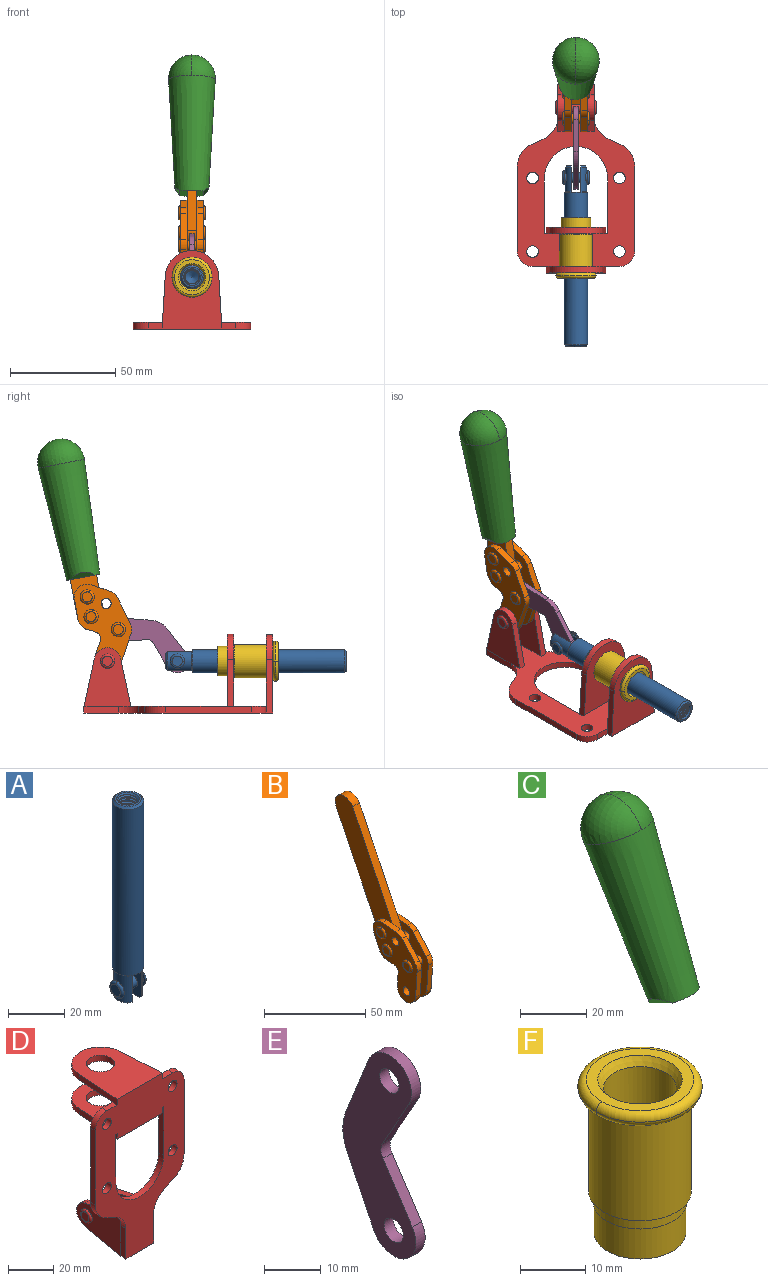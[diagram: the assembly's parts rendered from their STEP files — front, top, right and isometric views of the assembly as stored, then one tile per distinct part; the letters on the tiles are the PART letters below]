
ASSEMBLY  parts=6 mates=6
PART A: 48 faces, bbox 12.6x11.1x86.1 mm
  f0: torus R=2.41mm, axis (-1,0,0), area 15mm2, adj f30,f32,f34
  f1: torus R=2.41mm, axis (-1,0,0), area 15mm2, adj f29,f31,f33
  f2: cylinder r=5.54mm len=72.39mm, axis (0,0,1), area 2518.5mm2, adj f3,f4,f42,f43
  f3: cone r=5.54mm half-angle=45deg, axis (0,0,1), area 7.6mm2, adj f2,f5,f41
  f4: cone r=5.54mm half-angle=45deg, axis (0,0,-1), area 34.9mm2, adj f2,f39
  f5: cylinder r=5.08mm len=11.48mm, axis (0,0,1), area 108.3mm2, adj f3,f7,f8,f41
  f6: cylinder r=2.41mm len=4.83mm, axis (-1,0,0), area 71.2mm2, adj f40,f41
  f7: cylinder r=2.41mm len=4.83mm, axis (-1,0,0), area 7.6mm2, adj f5,f34
  f8: cone r=5.08mm half-angle=45deg, axis (0,0,1), area 10.6mm2, adj f5,f37,f41
  f9: cone r=3.98mm half-angle=45deg, axis (0,0,1), area 17.6mm2, adj f27,f39,f45,f46,f47
  f10: cylinder r=2.41mm len=4.83mm, axis (-1,0,0), area 7.6mm2, adj f33,f38
  f11: cylinder r=3.2mm len=6.4mm, axis (0,0,1), area 78.4mm2, adj f12,f28,f44,f45,f47
  f12: cylinder r=3.2mm len=6.4mm, axis (0,0,1), area 10.5mm2, adj f11,f13,f45,f47
  f13: cylinder r=3.2mm len=6.4mm, axis (0,0,1), area 10.5mm2, adj f12,f14,f45,f47
  f14: cylinder r=3.2mm len=6.4mm, axis (0,0,1), area 10.5mm2, adj f13,f15,f45,f47
  f15: cylinder r=3.2mm len=6.4mm, axis (0,0,1), area 10.5mm2, adj f14,f16,f45,f47
  f16: cylinder r=3.2mm len=6.4mm, axis (0,0,1), area 10.5mm2, adj f15,f17,f45,f47
  f17: cylinder r=3.2mm len=6.4mm, axis (0,0,1), area 10.5mm2, adj f16,f18,f45,f47
  f18: cylinder r=3.2mm len=6.4mm, axis (0,0,1), area 10.5mm2, adj f17,f19,f45,f47
  f19: cylinder r=3.2mm len=6.4mm, axis (0,0,1), area 10.5mm2, adj f18,f20,f45,f47
  f20: cylinder r=3.2mm len=6.4mm, axis (0,0,1), area 10.5mm2, adj f19,f21,f45,f47
  f21: cylinder r=3.2mm len=6.4mm, axis (0,0,1), area 10.5mm2, adj f20,f22,f45,f47
  f22: cylinder r=3.2mm len=6.4mm, axis (0,0,1), area 10.5mm2, adj f21,f23,f45,f47
  f23: cylinder r=3.2mm len=6.4mm, axis (0,0,1), area 10.5mm2, adj f22,f24,f45,f47
  f24: cylinder r=3.2mm len=6.4mm, axis (0,0,1), area 10.5mm2, adj f23,f25,f45,f47
  f25: cylinder r=3.2mm len=6.4mm, axis (0,0,1), area 10.5mm2, adj f24,f26,f45,f47
  f26: cylinder r=3.2mm len=6.4mm, axis (0,0,1), area 10.5mm2, adj f25,f27,f45,f47
  f27: cylinder r=3.2mm len=6.4mm, axis (0,0,1), area 7.4mm2, adj f9,f26,f45,f47
  f28: cone r=3.2mm half-angle=60deg, axis (0,0,1), area 37.2mm2, adj f11
  f29: plane 4.83x4.83mm, normal (-1,0,0), area 18.3mm2, adj f1,f31
  f30: plane 4.83x4.83mm, normal (1,0,0), area 18.3mm2, adj f0,f32
  f31: torus R=2.41mm, axis (-1,0,0), area 15mm2, adj f1,f29,f33
  f32: torus R=2.41mm, axis (-1,0,0), area 15mm2, adj f0,f30,f34
  f33: plane 6.83x6.83mm, normal (1,0,0), area 18.3mm2, adj f1,f10,f31
  f34: plane 6.83x6.83mm, normal (-1,0,0), area 18.3mm2, adj f0,f7,f32
  f35: cone r=5.08mm half-angle=45deg, axis (0,0,1), area 10.6mm2, adj f36,f38,f40
  f36: plane 7.25x1.97mm, normal (0,0,-1), area 10mm2, adj f35,f40
  f37: plane 7.25x1.97mm, normal (0,0,-1), area 10mm2, adj f8,f41
  f38: cylinder r=5.08mm len=11.48mm, axis (0,0,1), area 108.3mm2, adj f10,f35,f40,f42
  f39: plane 9.55x9.55mm, normal (0,0,1), area 22mm2, adj f4,f9
  f40: plane 12.76x10.09mm, normal (1,0,0), area 95.7mm2, adj f6,f35,f36,f38,f42,f43
  f41: plane 12.76x10.09mm, normal (-1,0,0), area 95.7mm2, adj f3,f5,f6,f8,f37,f43
  f42: cone r=5.54mm half-angle=45deg, axis (0,0,1), area 7.6mm2, adj f2,f38,f40
  f43: plane 11.07x4.7mm, normal (0,0,-1), area 50.4mm2, adj f2,f40,f41
  f44: plane 0.89x0.62mm, normal (-1,0,0), area 0.3mm2, adj f11,f45,f46,f47
  f45: bspline ~24.8x7.63mm, area 266.6mm2, adj f9,f11,f12,f13,f14,f15,f16,f17
  f46: bspline ~24.87x7.63mm, area 73.6mm2, adj f9,f44,f45,f47
  f47: bspline ~24.98x7.63mm, area 272.5mm2, adj f9,f11,f12,f13,f14,f15,f16,f17
PART B: 59 faces, bbox 12.9x60.2x99.6 mm
  f0: torus R=2.39mm, axis (-1,0,0), area 14.9mm2, adj f20,f43,f51
  f1: torus R=2.39mm, axis (-1,0,0), area 14.9mm2, adj f19,f42,f51
  f2: torus R=2.39mm, axis (-1,0,0), area 14.9mm2, adj f18,f35,f51
  f3: torus R=2.39mm, axis (-1,0,0), area 14.9mm2, adj f14,f17,f23
  f4: torus R=2.39mm, axis (-1,0,0), area 14.9mm2, adj f13,f16,f23
  f5: torus R=2.39mm, axis (-1,0,0), area 14.9mm2, adj f12,f15,f23
  f6: cylinder r=2.39mm len=4.78mm, axis (1,0,0), area 46.5mm2, adj f48,f50,f51
  f7: cylinder r=2.39mm len=4.78mm, axis (1,0,0), area 46.5mm2, adj f50,f51
  f8: cylinder r=6.35mm len=12.68mm, axis (1,0,0), area 61.8mm2, adj f38,f39,f50,f51
  f9: cylinder r=2.39mm len=4.78mm, axis (-1,0,0), area 70.5mm2, adj f46,f50
  f10: cylinder r=2.39mm len=4.78mm, axis (-1,0,0), area 46.5mm2, adj f23,f45,f46
  f11: cylinder r=2.39mm len=4.78mm, axis (-1,0,0), area 46.5mm2, adj f23,f46
  f12: plane 4.78x4.78mm, normal (1,0,0), area 17.9mm2, adj f5,f15
  f13: plane 4.78x4.78mm, normal (1,0,0), area 17.9mm2, adj f4,f16
  f14: plane 4.78x4.78mm, normal (1,0,0), area 17.9mm2, adj f3,f17
  f15: torus R=2.39mm, axis (-1,0,0), area 14.9mm2, adj f5,f12,f23
  f16: torus R=2.39mm, axis (-1,0,0), area 14.9mm2, adj f4,f13,f23
  f17: torus R=2.39mm, axis (-1,0,0), area 14.9mm2, adj f3,f14,f23
  f18: plane 4.78x4.78mm, normal (-1,0,0), area 17.9mm2, adj f2,f35
  f19: plane 4.78x4.78mm, normal (-1,0,0), area 17.9mm2, adj f1,f42
  f20: plane 4.78x4.78mm, normal (-1,0,0), area 17.9mm2, adj f0,f43
  f21: plane 2.26x0.2mm, normal (1,0,0), area 0.2mm2, adj f31,f44
  f22: plane 2.26x0.2mm, normal (-1,0,0), area 0.2mm2, adj f41,f44
  f23: plane 39.37x30.77mm, normal (1,0,0), area 565.5mm2, adj f3,f4,f5,f10,f11,f15,f16,f17
  f24: cylinder r=6.1mm len=4.15mm, axis (-1,0,0), area 14.7mm2, adj f23,f25,f32,f46
  f25: plane 10.25x9.01mm, normal (0,-0.75,0.66), area 42.3mm2, adj f23,f24,f26,f46
  f26: cylinder r=6.35mm len=4.64mm, axis (-1,0,0), area 15.6mm2, adj f23,f25,f27,f46
  f27: plane 15.84x3.1mm, normal (0,-1,-0.07), area 49.2mm2, adj f23,f26,f28,f46
  f28: cylinder r=6.35mm len=12.68mm, axis (-1,0,0), area 61.8mm2, adj f23,f27,f29,f46
  f29: plane 8.11x3.1mm, normal (0,1,0.07), area 25.2mm2, adj f23,f28,f30,f46
  f30: cylinder r=3.05mm len=3.25mm, axis (-1,0,0), area 14.8mm2, adj f23,f29,f31,f46
  f31: plane 5.99x3.1mm, normal (0,0.07,-1), area 18.6mm2, adj f21,f23,f30,f44,f46
  f32: plane 9.5x3.1mm, normal (0,-0.07,1), area 29.5mm2, adj f23,f24,f33,f46,f47
  f33: cylinder r=6.1mm len=8.63mm, axis (-1,0,0), area 39.1mm2, adj f23,f32,f34,f47
  f34: plane 8.65x3.96mm, normal (0,0.91,-0.42), area 29.5mm2, adj f23,f33,f44,f47
  f35: torus R=2.39mm, axis (-1,0,0), area 14.9mm2, adj f2,f18,f51
  f36: plane 10.25x9.01mm, normal (0,-0.75,0.66), area 42.3mm2, adj f37,f49,f50,f51
  f37: cylinder r=6.35mm len=4.64mm, axis (1,0,0), area 15.6mm2, adj f36,f38,f50,f51
  f38: plane 15.84x3.1mm, normal (0,-1,-0.07), area 49.2mm2, adj f8,f37,f50,f51
  f39: plane 8.11x3.1mm, normal (0,1,0.07), area 25.2mm2, adj f8,f40,f50,f51
  f40: cylinder r=3.05mm len=3.25mm, axis (1,0,0), area 14.8mm2, adj f39,f41,f50,f51
  f41: plane 5.99x3.1mm, normal (0,0.07,-1), area 18.6mm2, adj f22,f40,f44,f50,f51
  f42: torus R=2.39mm, axis (-1,0,0), area 14.9mm2, adj f1,f19,f51
  f43: torus R=2.39mm, axis (-1,0,0), area 14.9mm2, adj f0,f20,f51
  f44: cylinder r=6.35mm len=12.12mm, axis (-1,0,0), area 128.9mm2, adj f21,f22,f23,f31,f34,f41,f46,f47
  f45: plane 2.65x1.35mm, normal (1,0,0), area 1mm2, adj f10,f55
  f46: plane 39.08x20.42mm, normal (-1,0,0), area 412.5mm2, adj f9,f10,f11,f24,f25,f26,f27,f28
  f47: plane 77.62x39.82mm, normal (1,0,0), area 850mm2, adj f32,f33,f34,f44,f53,f54,f55
  f48: plane 2.65x1.35mm, normal (-1,0,0), area 1mm2, adj f6,f55
  f49: cylinder r=6.1mm len=4.15mm, axis (1,0,0), area 14.7mm2, adj f36,f50,f51,f56
  f50: plane 39.08x20.42mm, normal (1,0,0), area 412.5mm2, adj f6,f7,f8,f9,f36,f37,f38,f39
  f51: plane 39.37x30.77mm, normal (-1,0,0), area 565.5mm2, adj f0,f1,f2,f6,f7,f8,f35,f36
  f52: plane 8.65x3.96mm, normal (0,0.91,-0.42), area 29.5mm2, adj f44,f51,f57,f58
  f53: plane 68.49x33.4mm, normal (0,0.9,-0.44), area 358.1mm2, adj f44,f47,f54,f58
  f54: cylinder r=6.35mm len=12.06mm, axis (1,0,0), area 93.7mm2, adj f47,f53,f55,f58
  f55: plane 68.49x33.4mm, normal (0,-0.9,0.44), area 358.1mm2, adj f44,f45,f46,f47,f48,f50,f54,f58
  f56: plane 9.5x3.1mm, normal (0,-0.07,1), area 29.5mm2, adj f49,f50,f51,f57,f58
  f57: cylinder r=6.1mm len=8.63mm, axis (1,0,0), area 39.1mm2, adj f51,f52,f56,f58
  f58: plane 77.62x39.82mm, normal (-1,0,0), area 850mm2, adj f44,f52,f53,f54,f55,f56,f57
PART C: 11 faces, bbox 22.3x42.6x64.5 mm
  f0: sphere r=11.13mm, area 411.4mm2, adj f1,f8
  f1: cone r=11.11mm half-angle=3.3deg, axis (0,0.44,0.9), area 3251.8mm2, adj f0,f7,f8,f9,f10
  f2: cylinder r=6.16mm len=11.7mm, axis (1,0,0), area 89.5mm2, adj f3,f4,f5,f6
  f3: plane 60.23x36.75mm, normal (-1,0,0), area 763.6mm2, adj f2,f4,f6,f10
  f4: plane 51.37x25.05mm, normal (0,0.9,-0.44), area 264.2mm2, adj f2,f3,f5,f10
  f5: plane 60.23x36.75mm, normal (1,0,0), area 763.6mm2, adj f2,f4,f6,f10
  f6: plane 51.37x25.05mm, normal (0,-0.9,0.44), area 264.2mm2, adj f2,f3,f5,f10
  f7: plane 9.95x5.95mm, normal (0.71,-0.31,-0.64), area 25.8mm2, adj f1,f10
  f8: sphere r=11.13mm, area 411.4mm2, adj f0,f1
  f9: plane 9.95x5.95mm, normal (-0.71,-0.31,-0.64), area 25.8mm2, adj f1,f10
  f10: plane 14.27x11.38mm, normal (0,-0.44,-0.9), area 106.7mm2, adj f1,f3,f4,f5,f6,f7,f9
PART D: 55 faces, bbox 55.7x37.4x89.8 mm
  f0: torus R=2.41mm, axis (-1,0,0), area 15mm2, adj f11,f15,f25
  f1: torus R=2.41mm, axis (-1,0,0), area 15mm2, adj f10,f12,f22
  f2: cylinder r=2.78mm len=5.56mm, axis (0,-1,0), area 54.2mm2, adj f30,f54
  f3: cylinder r=14.99mm len=29.97mm, axis (0,-1,0), area 145.9mm2, adj f30,f49,f53,f54
  f4: cylinder r=2.78mm len=5.56mm, axis (0,-1,0), area 54.2mm2, adj f30,f54
  f5: cylinder r=2.78mm len=5.56mm, axis (0,-1,0), area 54.2mm2, adj f30,f54
  f6: cylinder r=2.78mm len=5.56mm, axis (0,-1,0), area 54.2mm2, adj f30,f54
  f7: cylinder r=6.35mm len=12.7mm, axis (0,0,1), area 123.6mm2, adj f27,f51
  f8: cylinder r=6.35mm len=12.7mm, axis (0,0,-1), area 124.7mm2, adj f21,f35
  f9: cylinder r=2.41mm len=11.18mm, axis (-1,0,0), area 169.4mm2, adj f16,f19
  f10: plane 4.83x4.83mm, normal (1,0,0), area 18.3mm2, adj f1,f12
  f11: plane 4.83x4.83mm, normal (-1,0,0), area 18.3mm2, adj f0,f15
  f12: torus R=2.41mm, axis (-1,0,0), area 15mm2, adj f1,f10,f22
  f13: cylinder r=6.35mm len=12.41mm, axis (1,0,0), area 53.4mm2, adj f18,f19,f22,f23
  f14: cylinder r=6.35mm len=12.41mm, axis (-1,0,0), area 53.4mm2, adj f16,f17,f24,f25
  f15: torus R=2.41mm, axis (-1,0,0), area 15mm2, adj f0,f11,f25
  f16: plane 27.86x22.35mm, normal (1,0,0), area 425.4mm2, adj f9,f14,f17,f24,f30
  f17: plane 22.86x4.97mm, normal (0,0.21,0.98), area 72.5mm2, adj f14,f16,f25,f30
  f18: plane 22.86x4.97mm, normal (0,0.21,0.98), area 72.5mm2, adj f13,f19,f22,f30
  f19: plane 27.86x22.35mm, normal (-1,0,0), area 425.4mm2, adj f9,f13,f18,f23,f30
  f20: cylinder r=12.7mm len=25.35mm, axis (0,0,-1), area 119.8mm2, adj f21,f34,f35,f36
  f21: plane 34.21x28.07mm, normal (0,0,-1), area 702.4mm2, adj f8,f20,f30,f34,f36
  f22: plane 27.96x22.45mm, normal (1,0,0), area 407.2mm2, adj f1,f12,f13,f18,f23,f30,f42,f43
  f23: plane 22.86x4.97mm, normal (0,0.21,-0.98), area 72.5mm2, adj f13,f19,f22,f44
  f24: plane 22.86x4.97mm, normal (0,0.21,-0.98), area 72.5mm2, adj f14,f16,f25,f44
  f25: plane 27.86x22.35mm, normal (-1,0,0), area 407.1mm2, adj f0,f14,f15,f17,f24,f30,f45,f46
  f26: plane 3.1x0.95mm, normal (0,0,-1), area 2.7mm2, adj f30,f49,f50,f54
  f27: plane 34.21x28.07mm, normal (0,0,1), area 702.4mm2, adj f7,f28,f30,f50,f52
  f28: cylinder r=12.7mm len=25.35mm, axis (0,0,1), area 118.8mm2, adj f27,f50,f51,f52
  f29: plane 3.1x0.95mm, normal (0,0,-1), area 2.7mm2, adj f30,f52,f53,f54
  f30: plane 86.54x55.63mm, normal (0,1,0), area 2362.9mm2, adj f2,f3,f4,f5,f6,f16,f17,f18
  f31: plane 40.56x3.1mm, normal (-1,0,0), area 125.7mm2, adj f30,f32,f48,f54
  f32: cylinder r=7.11mm len=7.11mm, axis (0,-1,0), area 34.6mm2, adj f30,f31,f33,f54
  f33: plane 6.67x3.1mm, normal (0,0,1), area 20.4mm2, adj f30,f32,f34,f54
  f34: plane 25.39x3.13mm, normal (-1,0.06,0), area 79.5mm2, adj f20,f21,f33,f35,f54
  f35: plane 37.31x28.45mm, normal (0,0,1), area 789.9mm2, adj f8,f20,f34,f36,f54
  f36: plane 25.39x3.13mm, normal (1,0.06,0), area 79.5mm2, adj f20,f21,f35,f37,f54
  f37: plane 6.67x3.1mm, normal (0,0,1), area 20.4mm2, adj f30,f36,f38,f54
  f38: cylinder r=7.11mm len=7.11mm, axis (0,-1,0), area 34.6mm2, adj f30,f37,f39,f54
  f39: plane 40.56x3.1mm, normal (1,0,0), area 125.7mm2, adj f30,f38,f40,f54
  f40: cylinder r=11.18mm len=10.16mm, axis (0,-1,0), area 39.5mm2, adj f30,f39,f41,f54
  f41: plane 6.09x3.1mm, normal (0.42,0,-0.91), area 20.8mm2, adj f30,f40,f42,f54
  f42: cylinder r=11.18mm len=9.41mm, axis (0,-1,0), area 37.2mm2, adj f22,f30,f41,f43,f54
  f43: plane 16.5x3.1mm, normal (1,0,0), area 51.1mm2, adj f22,f42,f44,f54
  f44: plane 17.37x3.1mm, normal (0,0,-1), area 53.8mm2, adj f23,f24,f30,f43,f45,f54
  f45: plane 16.5x3.1mm, normal (-1,0,0), area 51.1mm2, adj f25,f44,f46,f54
  f46: cylinder r=11.18mm len=9.41mm, axis (0,-1,0), area 37.2mm2, adj f25,f30,f45,f47,f54
  f47: plane 6.09x3.1mm, normal (-0.42,0,-0.91), area 20.8mm2, adj f30,f46,f48,f54
  f48: cylinder r=11.18mm len=10.16mm, axis (0,-1,0), area 39.5mm2, adj f30,f31,f47,f54
  f49: plane 26.54x3.1mm, normal (-1,0,0), area 82.3mm2, adj f3,f26,f30,f54
  f50: plane 25.39x3.1mm, normal (1,0.06,0), area 78.8mm2, adj f26,f27,f28,f51,f54
  f51: plane 37.31x28.45mm, normal (0,0,-1), area 789.9mm2, adj f7,f28,f50,f52,f54
  f52: plane 25.39x3.1mm, normal (-1,0.06,0), area 78.8mm2, adj f27,f28,f29,f51,f54
  f53: plane 26.54x3.1mm, normal (1,0,0), area 82.3mm2, adj f3,f29,f30,f54
  f54: plane 89.66x55.63mm, normal (0,-1,0), area 2678.5mm2, adj f2,f3,f4,f5,f6,f26,f29,f31
PART E: 12 faces, bbox 2.3x18.2x42.8 mm
  f0: cylinder r=2.4mm len=4.8mm, axis (1,0,0), area 34.9mm2, adj f4,f11
  f1: cylinder r=10.41mm len=8.47mm, axis (1,0,0), area 20.2mm2, adj f4,f9,f10,f11
  f2: cylinder r=3.05mm len=3.16mm, axis (1,0,0), area 7.7mm2, adj f4,f6,f7,f11
  f3: cylinder r=2.4mm len=4.8mm, axis (1,0,0), area 34.9mm2, adj f4,f11
  f4: plane 42.81x18.23mm, normal (-1,0,0), area 414.1mm2, adj f0,f1,f2,f3,f5,f6,f7,f8
  f5: cylinder r=5.54mm len=10.67mm, axis (1,0,0), area 41.8mm2, adj f4,f6,f10,f11
  f6: plane 11.66x6.53mm, normal (0,-0.87,-0.49), area 30.9mm2, adj f2,f4,f5,f11
  f7: plane 11.17x7.33mm, normal (0,-0.84,0.55), area 30.9mm2, adj f2,f4,f8,f11
  f8: cylinder r=5.54mm len=10.51mm, axis (1,0,0), area 41.8mm2, adj f4,f7,f9,f11
  f9: plane 13.67x6.67mm, normal (0,0.9,-0.44), area 35.1mm2, adj f1,f4,f8,f11
  f10: plane 14.1x5.7mm, normal (0,0.93,0.37), area 35.1mm2, adj f1,f4,f5,f11
  f11: plane 42.81x18.23mm, normal (1,0,0), area 414.1mm2, adj f0,f1,f2,f3,f5,f6,f7,f8
PART F: 15 faces, bbox 20.6x20.6x28.7 mm
  f0: torus R=8.26mm, axis (0,0,1), area 56.8mm2, adj f1,f10,f12
  f1: torus R=8.26mm, axis (0,0,1), area 56.8mm2, adj f0,f6,f13
  f2: cylinder r=5.59mm len=25.91mm, axis (0,0,1), area 909.6mm2, adj f3,f4
  f3: cone r=6.86mm half-angle=45deg, axis (0,0,-1), area 70.2mm2, adj f2,f14
  f4: cone r=6.47mm half-angle=30deg, axis (0,0,1), area 66.7mm2, adj f2,f13
  f5: cylinder r=7.04mm len=14.07mm, axis (0,0,1), area 252.6mm2, adj f11,f14
  f6: torus R=8.26mm, axis (0,0,1), area 56.8mm2, adj f1,f12,f13
  f7: cylinder r=7.16mm len=14.33mm, axis (0,0,1), area 91.5mm2, adj f9,f11
  f8: cylinder r=7.86mm len=18.42mm, axis (0,0,1), area 909.6mm2, adj f9,f10
  f9: plane 15.72x15.72mm, normal (0,0,-1), area 33mm2, adj f7,f8
  f10: plane 16.51x16.51mm, normal (0,0,-1), area 19.9mm2, adj f0,f8,f12
  f11: plane 14.33x14.33mm, normal (0,0,-1), area 5.7mm2, adj f5,f7
  f12: torus R=8.26mm, axis (0,0,1), area 56.8mm2, adj f0,f6,f10
  f13: plane 16.51x16.51mm, normal (0,0,1), area 82.7mm2, adj f1,f4,f6
  f14: plane 14.07x14.07mm, normal (0,0,-1), area 7.8mm2, adj f3,f5
PLACE A rot(axis=(1,0,0),90deg) t=(0,23.56,0)mm
PLACE B rot(axis=(1,0,0),15deg) t=(0,9.15,49.24)mm
PLACE C rot(axis=(1,0,0),15deg) t=(-0.04,9.15,49.24)mm
PLACE D rot(axis=(1,0,0),90deg) t=(0,9.14,0)mm fixed
PLACE E rot(axis=(1,0,0),120.2deg) t=(0,33.84,11.13)mm
PLACE F rot(axis=(1,0,0),90deg) t=(0,9.14,0)mm
MATE revolute E.f3 <-> B.f4  axis (1,0,0) through (0,36.06,39.62)mm
MATE fastened F.f2 <-> D.f7  axis (0,1,0) through (0,-37.25,24.61)mm
MATE revolute E.f5 <-> A.f6  axis (1,0,0) through (0,8.09,24.61)mm
MATE slider A.f2 <-> D.f7  axis (0,-1,0) through (0,-35.22,24.61)mm
MATE revolute B.f7 <-> D.f0  axis (-1,0,0) through (0,41.23,24.61)mm
MATE fastened C.f2 <-> B.f54  axis (1,0,0) through (-2.35,63.6,120.54)mm
